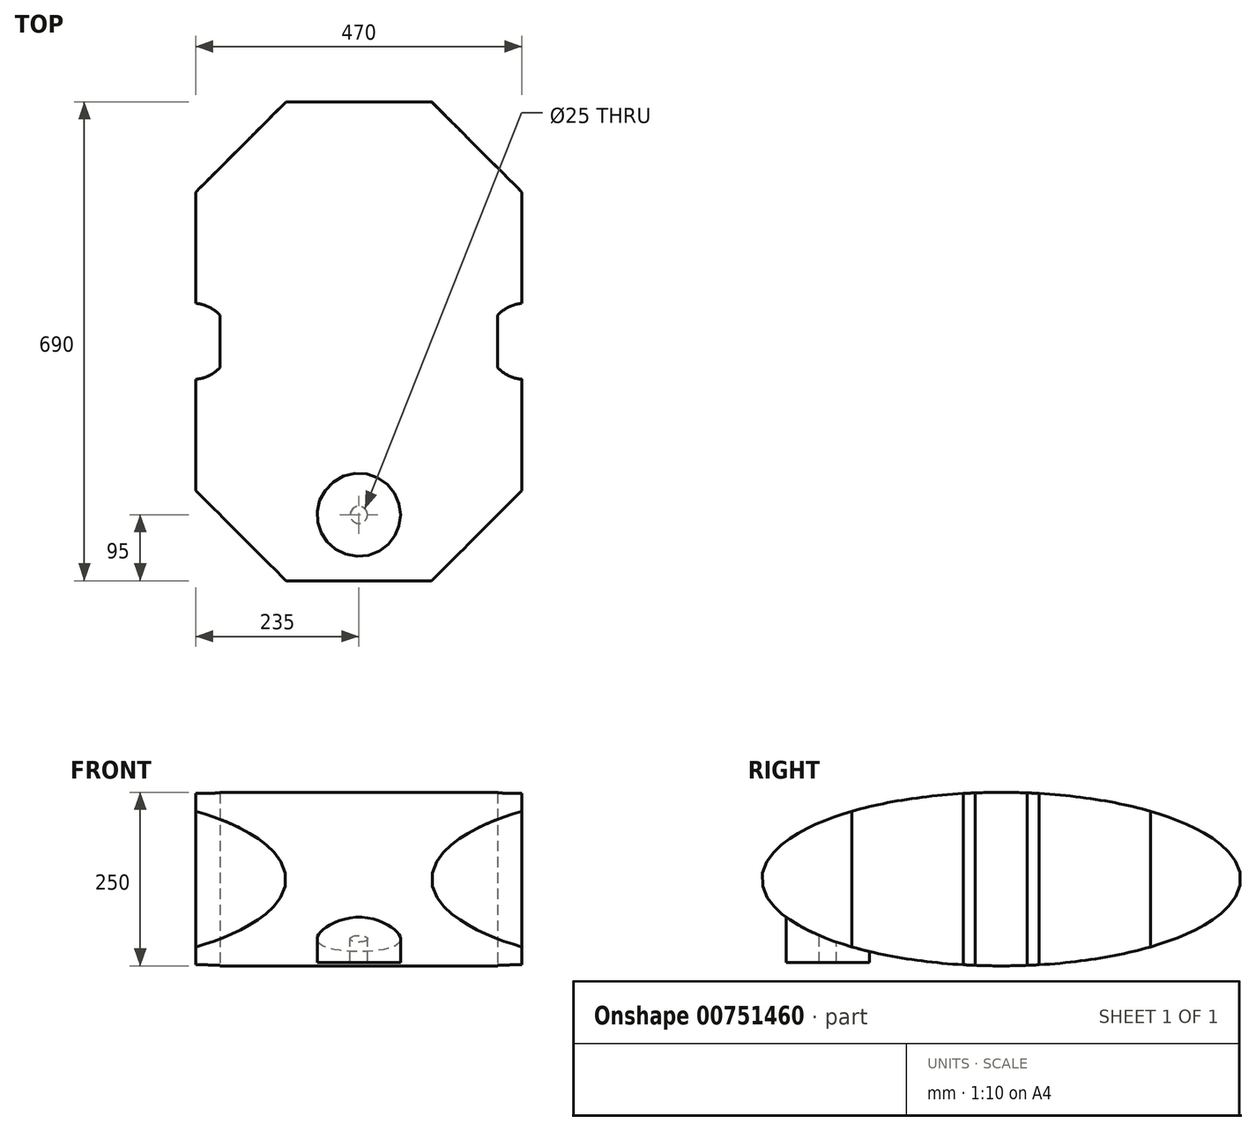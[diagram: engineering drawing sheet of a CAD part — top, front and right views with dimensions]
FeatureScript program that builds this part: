
annotation { "Feature Type Name" : "Feature", "Feature Type Description" : "" }
export const myFeature = defineFeature(function(context is Context, id is Id, definition is map)
    precondition{}
    {
        {
            var Q0;
            Q0=qCreatedBy(makeId("Right.planeOp"),FACE);
            var sketch = newSketch(context, id + "F0", { "sketchPlane" : qUnion([Q0])});
            skEllipse(sketch, "E0", {"center": v(0, 0) * mm, "majorRadius": 345 * mm, "minorRadius": 125 * mm, "majorAxis": v(1, 0)});
            skSolve(sketch);
        }
        {
            var Q0;
            Q0=makeQuery(id+"F0.imprint","IMPRINT",FACE,{"disambiguationData":[TD([[makeQuery(id+"F0.imprint","IMPRINT",EDGE,{"derivedFrom":sQuery(id+"F0.wireOp",EDGE,"E0")}),1.0]])]});
            extrude(context, id + "F1", {"entities" : qUnion([Q0]), "endBound" : BoundingType.SYMMETRIC, "depth" : 470 * mm, "offsetDistance" : 25 * mm});
        }
        {
            var Q0;
            Q0=qCreatedBy(makeId("Top.planeOp"),FACE);
            var sketch = newSketch(context, id + "F2", { "sketchPlane" : qUnion([Q0])});
            skLineSegment(sketch, "E1.bottom", {"start": v(-365, 450) * mm, "end": v(365, 450) * mm});
            skLineSegment(sketch, "E1.top", {"start": v(-365, -450) * mm, "end": v(365, -450) * mm});
            skLineSegment(sketch, "E1.left", {"start": v(-365, 450) * mm, "end": v(-365, 85) * mm});
            skLineSegment(sketch, "E1.right", {"start": v(365, 450) * mm, "end": v(365, 85) * mm});
            skLineSegment(sketch, "E2", {"start": v(0, 450) * mm, "end": v(365, 85) * mm});
            skLineSegment(sketch, "E3", {"start": v(0, 450) * mm, "end": v(0, -450) * mm, "construction": true});
            skLineSegment(sketch, "E4", {"start": v(-365, 0) * mm, "end": v(365, 0) * mm, "construction": true});
            skLineSegment(sketch, "E5.MirrorCS", {"start": v(0, 450) * mm, "end": v(-365, 85) * mm});
            skLineSegment(sketch, "E6.MirrorCS", {"start": v(0, -450) * mm, "end": v(-365, -85) * mm});
            skLineSegment(sketch, "E7.MirrorCS", {"start": v(0, -450) * mm, "end": v(365, -85) * mm});
            skLineSegment(sketch, "E8.trimOffspring", {"start": v(-365, -85) * mm, "end": v(-365, -450) * mm});
            skLineSegment(sketch, "E9.trimOffspring", {"start": v(365, -85) * mm, "end": v(365, -450) * mm});
            skSolve(sketch);
        }
        {
            var Q0;
            {var subQ0=sQuery(id+"F2.wireOp",EDGE,"E1.left");Q0=makeQuery(id+"F2.imprint","IMPRINT",FACE,{"disambiguationData":[TD([[makeQuery(id+"F2.imprint","IMPRINT",EDGE,{"derivedFrom":subQ0}),1.0]])]});}
            var Q1;
            {var subQ2=sQuery(id+"F2.wireOp",EDGE,"E6.MirrorCS");Q1=makeQuery(id+"F2.imprint","IMPRINT",FACE,{"disambiguationData":[TD([[makeQuery(id+"F2.imprint","IMPRINT",EDGE,{"derivedFrom":subQ2}),1.0]])]});}
            var Q2;
            {var subQ2=sQuery(id+"F2.wireOp",EDGE,"E7.MirrorCS");Q2=makeQuery(id+"F2.imprint","IMPRINT",FACE,{"disambiguationData":[TD([[makeQuery(id+"F2.imprint","IMPRINT",EDGE,{"derivedFrom":subQ2}),-1.0]])]});}
            var Q3;
            {var subQ0=sQuery(id+"F2.wireOp",EDGE,"E1.right");Q3=makeQuery(id+"F2.imprint","IMPRINT",FACE,{"disambiguationData":[TD([[makeQuery(id+"F2.imprint","IMPRINT",EDGE,{"derivedFrom":subQ0}),-1.0]])]});}
            extrude(context, id + "F3", {"entities" : qUnion([Q0, Q1, Q2, Q3]), "operationType" : NewBodyOperationType.REMOVE, "endBound" : BoundingType.THROUGH_ALL, "oppositeDirection" : true, "depth" : 25 * mm, "offsetDistance" : 25 * mm, "hasSecondDirection" : true, "secondDirectionBound" : SecondDirectionBoundingType.THROUGH_ALL, "secondDirectionOppositeDirection" : false, "secondDirectionDepth" : 25 * mm});
        }
        {
            var Q0;
            Q0=qCreatedBy(makeId("Top.planeOp"),FACE);
            var sketch = newSketch(context, id + "F4", { "sketchPlane" : qUnion([Q0])});
            skArc(sketch, "E10", {"start": v(-200, 37.75) * mm, "mid": v(-295, 0) * mm, "end": v(-200, -37.75) * mm});
            skLineSegment(sketch, "E11", {"start": v(0, 25) * mm, "end": v(0, -25) * mm, "construction": true});
            skArc(sketch, "E12.MirrorC", {"start": v(200, 37.75) * mm, "mid": v(295, 0) * mm, "end": v(200, -37.75) * mm});
            skLineSegment(sketch, "E13", {"start": v(-200, 37.75) * mm, "end": v(-200, -37.75) * mm});
            skLineSegment(sketch, "E14.MirrorCS", {"start": v(200, 37.75) * mm, "end": v(200, -37.75) * mm});
            skSolve(sketch);
        }
        {
            var Q0;
            Q0 = qSketchRegion(id + "F4", true);
            var Q1;
            Q1=makeQuery(id+"F1.opExtrude","SWEPT_BODY",BODY,{"disambiguationData":[OSD([sQuery(id+"F0.wireOp",EDGE,"E0")])]});
            var Q2;
            Q2=makeQuery(id+"F1.opExtrude","SWEPT_BODY",BODY,{"disambiguationData":[OSD([sQuery(id+"F0.wireOp",EDGE,"E0")])]});
            extrude(context, id + "F5", {"entities" : qUnion([Q0]), "operationType" : NewBodyOperationType.REMOVE, "endBound" : BoundingType.THROUGH_ALL, "depth" : 25 * mm, "endBoundEntityBody" : qUnion([Q1]), "offsetDistance" : 25 * mm, "hasSecondDirection" : true, "secondDirectionBound" : SecondDirectionBoundingType.UP_TO_BODY, "secondDirectionOppositeDirection" : true, "secondDirectionDepth" : 25 * mm, "secondDirectionBoundEntityBody" : qUnion([Q2])});
        }
        {
            var Q0;
            Q0=qCreatedBy(makeId("Top.planeOp"),FACE);
            var sketch = newSketch(context, id + "F6", { "sketchPlane" : qUnion([Q0])});
            skCircle(sketch, "E15", {"center": v(0, -250) * mm, "radius": 60 * mm});
            skCircle(sketch, "E16", {"center": v(0, -250) * mm, "radius": 12.5 * mm});
            skLineSegment(sketch, "E17", {"start": v(0, 0) * mm, "end": v(0, -250) * mm, "construction": true});
            skSolve(sketch);
        }
        {
            var Q0;
            Q0 = qSketchRegion(id + "F6", true);
            extrude(context, id + "F7", {"entities" : qUnion([Q0]), "operationType" : NewBodyOperationType.ADD, "oppositeDirection" : true, "depth" : 120 * mm, "offsetDistance" : 25 * mm});
        }
    });
